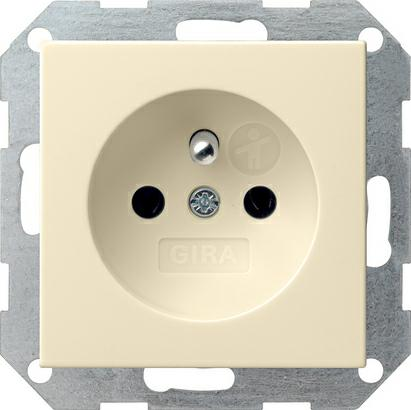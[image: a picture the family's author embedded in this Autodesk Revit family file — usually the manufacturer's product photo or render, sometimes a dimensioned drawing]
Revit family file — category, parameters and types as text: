
# Revit family: E_Cable Junction Box_F_MEPcontent_Spelsberg_BS 1_INT-EN
name_source: partatom
category: Electrical Fixtures
revit_build: Autodesk Revit 2017 (Build: 20160225_1515(x64)
units: mm (PartAtom-declared; Revit-internal decimal feet)

## family parameters
Cut with Voids When Loaded = No
Host = Face
Maintain Annotation Orientation = Yes
OmniClass Number = 23.80.30.14.24
OmniClass Title = Junction Boxes
Part Type = Junction Box
Room Calculation Point = No
Round Connector Dimension = Use Diameter
Shared = No

## types (1)
- BS 1
    3D Representation = 3DGeometry
    Article Description = Equipment installation box BS 1
    Article Type = BS 1
    Blue = Color RAL 5013
    Default Elevation = 0 mm  [stored 0 ft]
    Description = Equipment installation box BS 1
    ETIM Article Class = EC002601
    Green = Color RAL 6018
    Height = 59.1 mm  [stored 0.193898 ft]
    IFCExportAs = IfcJunctionBox
    IFCExportType = NOTDEFINED
    Length = 86 mm  [stored 0.282152 ft]
    Manufacturer = Spelsberg
    Manufacturer Art. No. = 97400101
    Manufacturer URL = http://www.spelsberg.com
    Model = BS 1
    Placeholder Height = 59.1 mm  [stored 0.193898 ft]
    Product Line = Spelsberg
    Revit Version = 2017
    Rotation U-Axis Correction = 0.00°
    Rotation U-Axis Default Correction = 0.00°
    Rotation V-Axis Correction = 0.00°
    Rotation V-Axis Default Correction = 0.00°
    Rotation W-Axis Correction = 0.00°
    Rotation W-Axis Default Correction = 0.00°
    Voltage = 230 V
    Width = 86 mm  [stored 0.282152 ft]

note: [stored X ft] marks values corroborated as IEEE doubles in the binary element streams (Revit-internal decimal feet)

## geometry (parser evidence)
native form markers: Sweep x14
no freeform markers — native parametric forms only
